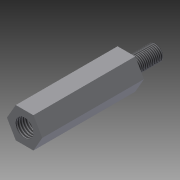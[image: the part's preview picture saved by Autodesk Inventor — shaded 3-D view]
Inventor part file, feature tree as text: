
AUTODESK INVENTOR PART (.ipt)
format: ipt  version: 2015 (Build 190159000, 159)  size: 90,624 bytes
history: native  units: mm
features: extrude x3, sketch x3, thread x2
ambient origin geometry x8: Origin, YZ Plane, XZ Plane, XY Plane, X Axis, Y Axis, Z Axis, Center Point
bodies: Solid1 (feature_tree)
feature tree (8):
  extrude  "Extrusion1"  Depth=20.0mm TaperAngle=0.0deg
  sketch  "Sketch2"  dims[d4=3.5mm d5=3.0mm]
  extrude  "Extrusion2"  Depth=3.0mm
  extrude  "Extrusion3"  Depth=6.0mm TaperAngle=0.0deg
  thread  "Thread1"  [1 undecoded]
  thread  "Thread2"  [1 undecoded]
  sketch  "Sketch1"  dims[d1=6.0mm d2=20.0mm d3=0.0mm]
  sketch  "Sketch3"  dims[d6=5.7mm d7=0.0mm d8=6.0mm d9=0.0mm d10=10.0mm d11=0.0mm d12=10.0mm d13=0.0mm]
note: 2 required parameter values undecoded (feature->parameter linkage not recoverable at this tier; creation-order binding heuristic only, values carry confidence <= 0.55)
